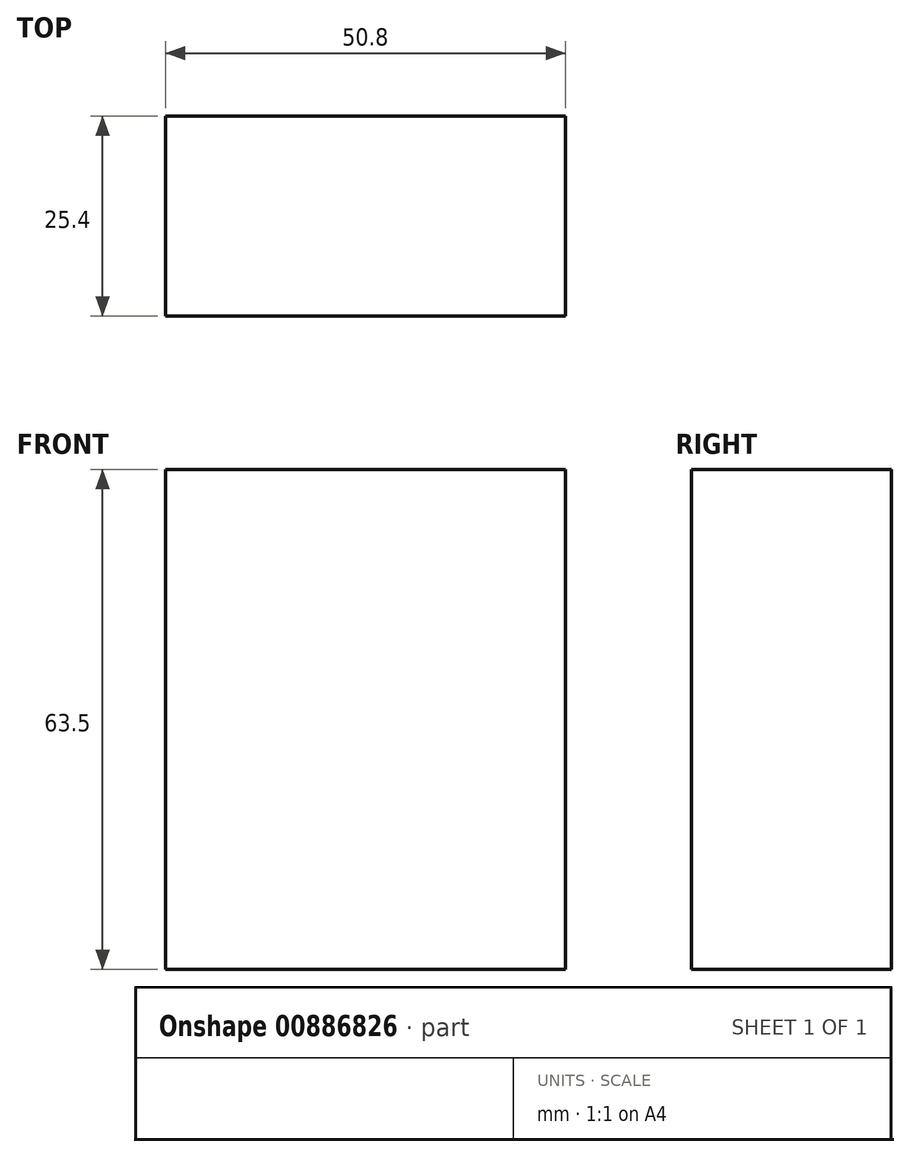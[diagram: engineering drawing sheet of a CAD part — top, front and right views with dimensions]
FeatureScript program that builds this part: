
annotation { "Feature Type Name" : "Feature", "Feature Type Description" : "" }
export const myFeature = defineFeature(function(context is Context, id is Id, definition is map)
    precondition{}
    {
        {
            var Q0;
            Q0=qCreatedBy(makeId("Front.planeOp"),FACE);
            var sketch = newSketch(context, id + "F0", { "sketchPlane" : qUnion([Q0])});
            skLineSegment(sketch, "E0.bottom", {"start": v(-12.99, 31) * mm, "end": v(37.81, 31) * mm});
            skLineSegment(sketch, "E0.top", {"start": v(-12.99, -32.5) * mm, "end": v(37.81, -32.5) * mm});
            skLineSegment(sketch, "E0.left", {"start": v(-12.99, 31) * mm, "end": v(-12.99, -32.5) * mm});
            skLineSegment(sketch, "E0.right", {"start": v(37.81, 31) * mm, "end": v(37.81, -32.5) * mm});
            skSolve(sketch);
        }
        {
            var Q0;
            Q0=makeQuery(id+"F0.imprint","IMPRINT",FACE,{"disambiguationData":[TD([[makeQuery(id+"F0.imprint","IMPRINT",EDGE,{"derivedFrom":sQuery(id+"F0.wireOp",EDGE,"E0.bottom")}),-1.0]])]});
            extrude(context, id + "F1", {"entities" : qUnion([Q0]), "depth" : 25.4 * mm, "offsetDistance" : 25.4 * mm});
        }
    });
